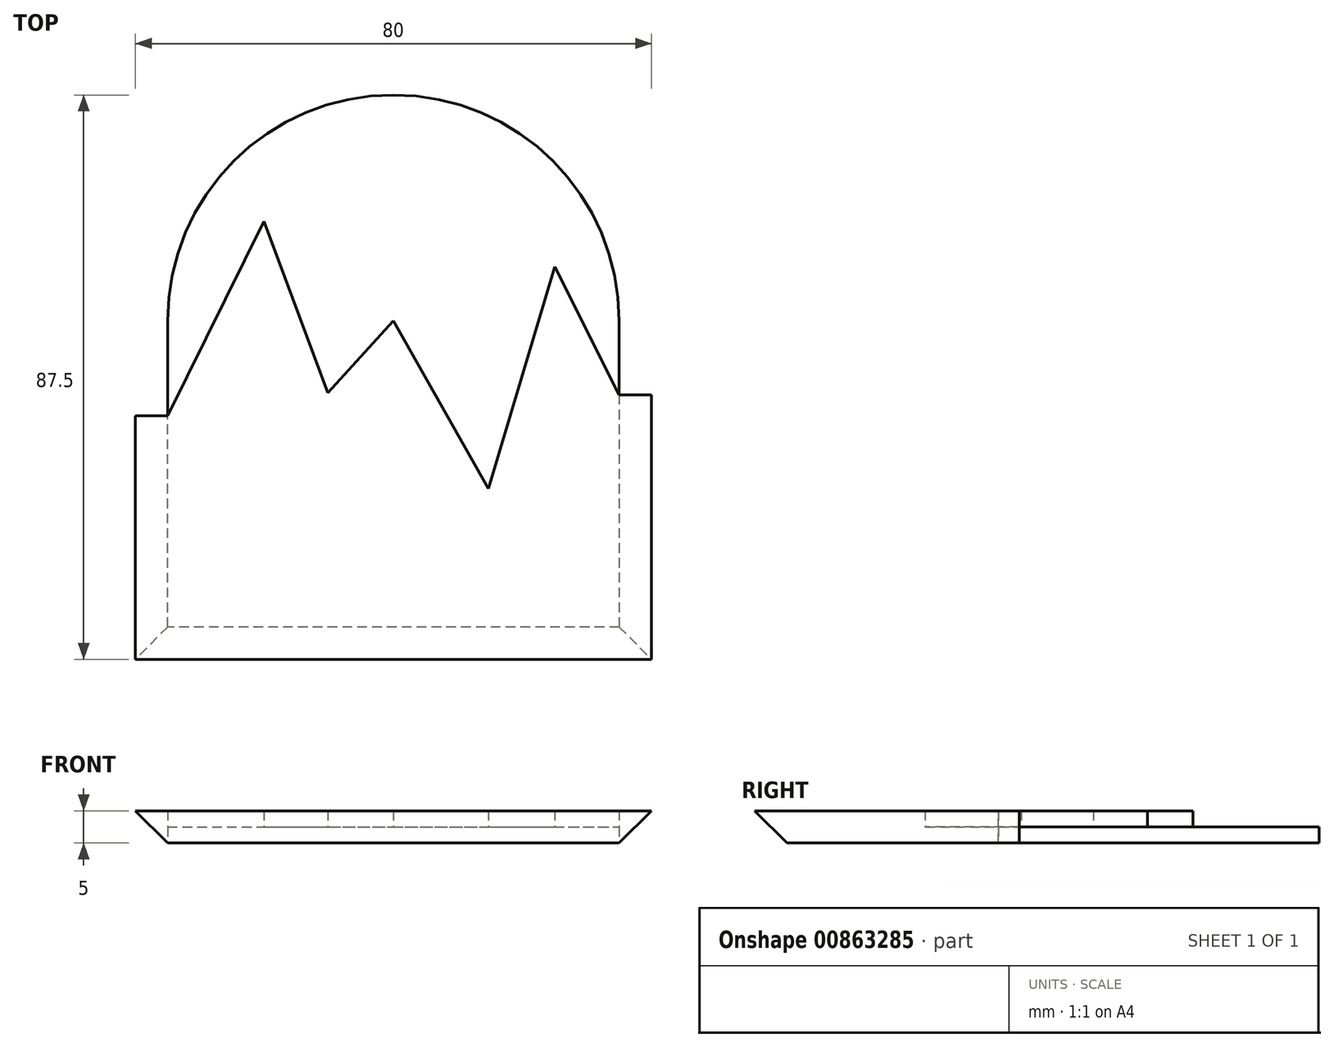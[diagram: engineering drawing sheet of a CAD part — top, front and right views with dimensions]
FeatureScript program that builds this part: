
annotation { "Feature Type Name" : "Feature", "Feature Type Description" : "" }
export const myFeature = defineFeature(function(context is Context, id is Id, definition is map)
    precondition{}
    {
        {
            var Q0;
            Q0=qCreatedBy(makeId("Top.planeOp"),FACE);
            var sketch = newSketch(context, id + "F0", { "sketchPlane" : qUnion([Q0])});
            skLineSegment(sketch, "E0.bottom", {"start": v(35, -47.5) * mm, "end": v(-35, -47.5) * mm});
            skLineSegment(sketch, "E0.top", {"start": v(35, 47.5) * mm, "end": v(-35, 47.5) * mm});
            skLineSegment(sketch, "E0.left", {"start": v(35, -47.5) * mm, "end": v(35, 47.5) * mm});
            skLineSegment(sketch, "E0.right", {"start": v(-35, -47.5) * mm, "end": v(-35, 47.5) * mm});
            skLineSegment(sketch, "E1.bottom", {"start": v(40, -52.5) * mm, "end": v(-40, -52.5) * mm});
            skLineSegment(sketch, "E1.top", {"start": v(40, 52.5) * mm, "end": v(-40, 52.5) * mm});
            skLineSegment(sketch, "E1.left", {"start": v(40, -52.5) * mm, "end": v(40, 52.5) * mm});
            skLineSegment(sketch, "E1.right", {"start": v(-40, -52.5) * mm, "end": v(-40, 52.5) * mm});
            skLineSegment(sketch, "E2", {"start": v(-35, -14.74) * mm, "end": v(-20.1, 15.44) * mm});
            skLineSegment(sketch, "E3", {"start": v(-20.1, 15.44) * mm, "end": v(-10.15, -11.19) * mm});
            skLineSegment(sketch, "E4", {"start": v(-10.15, -11.19) * mm, "end": v(0, 0) * mm});
            skLineSegment(sketch, "E5", {"start": v(0, 0) * mm, "end": v(14.7, -26.06) * mm});
            skLineSegment(sketch, "E6", {"start": v(14.7, -26.06) * mm, "end": v(25, 8.38) * mm});
            skLineSegment(sketch, "E7", {"start": v(25, 8.38) * mm, "end": v(35, -11.5) * mm});
            skLineSegment(sketch, "E8", {"start": v(35, -11.5) * mm, "end": v(40, -11.5) * mm});
            skLineSegment(sketch, "E9", {"start": v(-35, -14.74) * mm, "end": v(-40, -14.74) * mm});
            skSolve(sketch);
        }
        {
            var Q0;
            {var subQ1=sQuery(id+"F0.wireOp",EDGE,"E0.bottom");Q0=makeQuery(id+"F0.imprint","IMPRINT",FACE,{"disambiguationData":[TD([[makeQuery(id+"F0.imprint","IMPRINT",EDGE,{"derivedFrom":subQ1}),-1.0]])]});}
            var Q1;
            {var subQ2=sQuery(id+"F0.wireOp",EDGE,"E0.bottom");Q1=makeQuery(id+"F0.imprint","IMPRINT",FACE,{"disambiguationData":[TD([[makeQuery(id+"F0.imprint","IMPRINT",EDGE,{"derivedFrom":subQ2}),1.0]])]});}
            extrude(context, id + "F1", {"entities" : qUnion([Q0, Q1]), "depth" : 5 * mm, "offsetDistance" : 25 * mm});
        }
        {
            var Q0;
            Q0=makeQuery(id+"F1.opExtrude","CAP_EDGE",EDGE,{"disambiguationData":[OSD([sQuery(id+"F0.wireOp",EDGE,"E1.left")])],"isStart":true});
            var Q1;
            Q1=makeQuery(id+"F1.opExtrude","CAP_EDGE",EDGE,{"disambiguationData":[OSD([sQuery(id+"F0.wireOp",EDGE,"E1.bottom")])],"isStart":true});
            var Q2;
            Q2=makeQuery(id+"F1.opExtrude","CAP_EDGE",EDGE,{"disambiguationData":[OSD([sQuery(id+"F0.wireOp",EDGE,"E1.right")])],"isStart":true});
            chamfer(context, id + "F2", {"entities" : qUnion([Q0, Q1, Q2]), "width" : 5 * mm, "tangentPropagation" : true});
        }
        {
            var Q0;
            Q0=makeQuery(id+"F1.opExtrude","CAP_FACE",FACE,{"disambiguationData":[OSD([sQuery(id+"F0.wireOp",EDGE,"E1.bottom"),sQuery(id+"F0.wireOp",EDGE,"E1.left"),sQuery(id+"F0.wireOp",EDGE,"E1.right"),sQuery(id+"F0.wireOp",EDGE,"E2"),sQuery(id+"F0.wireOp",EDGE,"E3"),sQuery(id+"F0.wireOp",EDGE,"E4"),sQuery(id+"F0.wireOp",EDGE,"E5"),sQuery(id+"F0.wireOp",EDGE,"E6"),sQuery(id+"F0.wireOp",EDGE,"E7"),sQuery(id+"F0.wireOp",EDGE,"E8"),sQuery(id+"F0.wireOp",EDGE,"E9")])],"isStart":true});
            var sketch = newSketch(context, id + "F3", { "sketchPlane" : qUnion([Q0])});
            skCircle(sketch, "E10", {"center": v(0, 0) * mm, "radius": 35 * mm});
            skLineSegment(sketch, "E11", {"start": v(-35, 14.74) * mm, "end": v(-35, 0) * mm});
            skLineSegment(sketch, "E12", {"start": v(35, 11.5) * mm, "end": v(35, 0) * mm});
            skLineSegment(sketch, "E13", {"start": v(-35, 14.74) * mm, "end": v(35, 14.74) * mm});
            skSolve(sketch);
        }
        {
            var Q0;
            {var subQ13=makeQuery(id+"F1.opExtrude","CAP_EDGE",EDGE,{"disambiguationData":[OSD([sQuery(id+"F0.wireOp",EDGE,"E3")])],"isStart":true});Q0=makeQuery(id+"F3.imprint","IMPRINT",FACE,{"disambiguationData":[TD([[makeQuery(id+"F3.imprint","IMPRINT",EDGE,{"derivedFrom":subQ13}),-1.0]])]});}
            var Q1;
            {var subQ0=sQuery(id+"F3.wireOp",EDGE,"E13");var subQ1=makeQuery(id+"F1.opExtrude","CAP_EDGE",EDGE,{"disambiguationData":[OSD([sQuery(id+"F0.wireOp",EDGE,"E5")])],"isStart":true});var subQ2=makeQuery(id+"F3.imprint","INTERSECT",VERTEX,{"derivedFrom":[subQ1,subQ0]});Q1=makeQuery(id+"F3.imprint","IMPRINT",FACE,{"disambiguationData":[TD([[makeQuery(id+"F3.imprint","IMPRINT",EDGE,{"disambiguationData":[TD([[subQ2,-1.0]])],"derivedFrom":subQ0}),1.0]])]});}
            var Q2;
            {var subQ0=sQuery(id+"F3.wireOp",EDGE,"E11");Q2=makeQuery(id+"F3.imprint","IMPRINT",FACE,{"disambiguationData":[TD([[makeQuery(id+"F3.imprint","IMPRINT",EDGE,{"derivedFrom":subQ0}),1.0]])]});}
            var Q3;
            {var subQ0=sQuery(id+"F3.wireOp",EDGE,"E12");Q3=makeQuery(id+"F3.imprint","IMPRINT",FACE,{"disambiguationData":[TD([[makeQuery(id+"F3.imprint","IMPRINT",EDGE,{"derivedFrom":subQ0}),-1.0]])]});}
            extrude(context, id + "F4", {"entities" : qUnion([Q0, Q1, Q2, Q3]), "operationType" : NewBodyOperationType.ADD, "oppositeDirection" : true, "depth" : 2.5 * mm, "offsetDistance" : 25 * mm});
        }
    });
